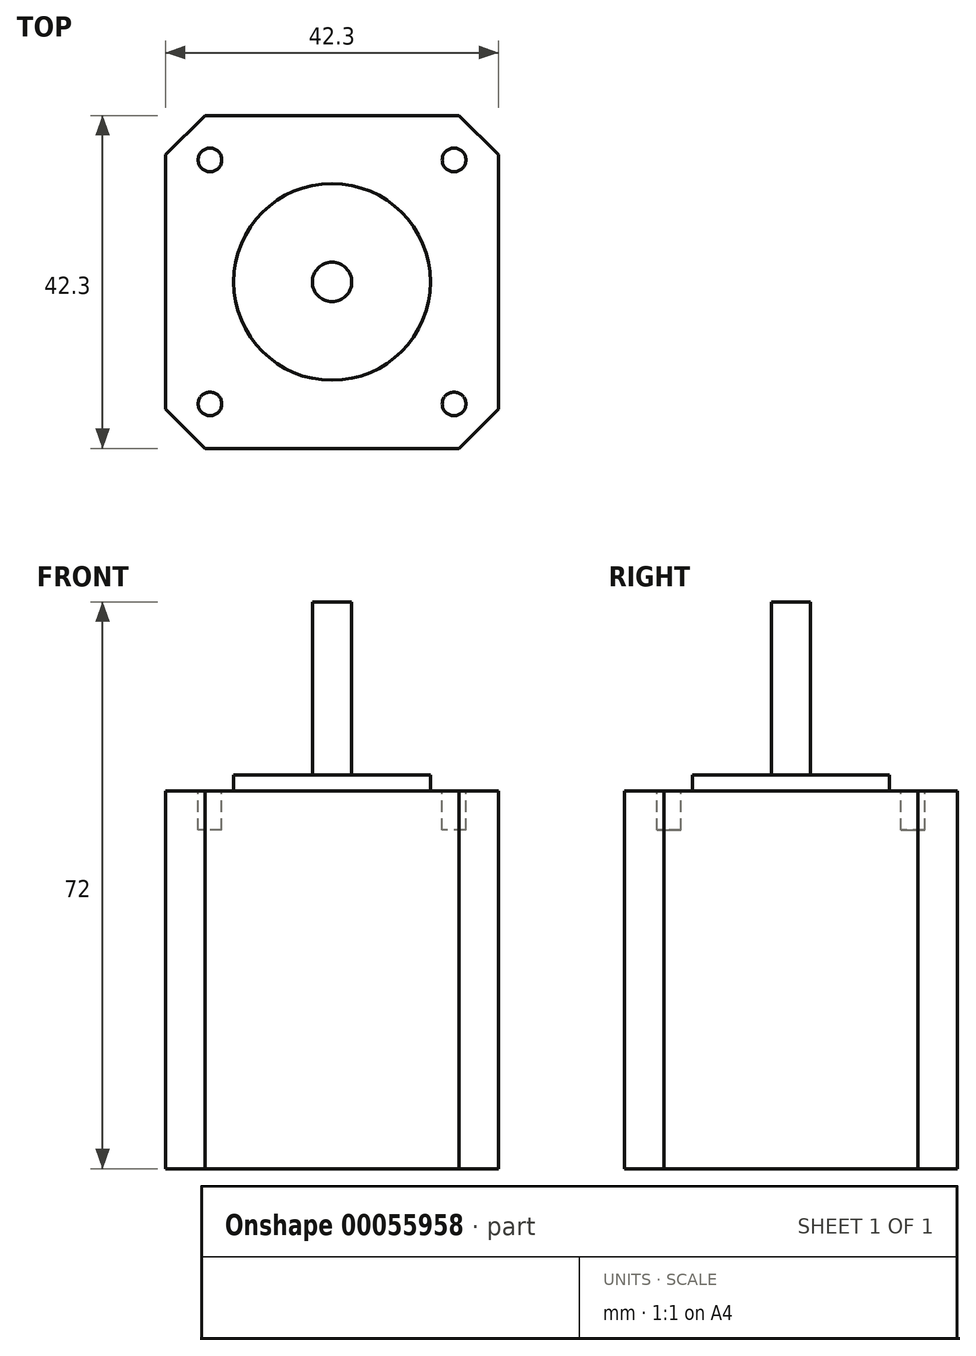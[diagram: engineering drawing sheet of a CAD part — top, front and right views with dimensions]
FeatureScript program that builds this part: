
annotation { "Feature Type Name" : "Feature", "Feature Type Description" : "" }
export const myFeature = defineFeature(function(context is Context, id is Id, definition is map)
    precondition{}
    {
        {
            var Q0;
            Q0=qCreatedBy(makeId("Top.planeOp"),FACE);
            var sketch = newSketch(context, id + "F0", { "sketchPlane" : qUnion([Q0])});
            skLineSegment(sketch, "E0.rect.bottom", {"start": v(21.15, 21.15) * mm, "end": v(-21.15, 21.15) * mm});
            skLineSegment(sketch, "E0.rect.top", {"start": v(21.15, -21.15) * mm, "end": v(-21.15, -21.15) * mm});
            skLineSegment(sketch, "E0.rect.left", {"start": v(21.15, 21.15) * mm, "end": v(21.15, -21.15) * mm});
            skLineSegment(sketch, "E0.rect.right", {"start": v(-21.15, 21.15) * mm, "end": v(-21.15, -21.15) * mm});
            skPoint(sketch, "E0.rect.middle", {"position": v(0, 0) * mm});
            skSolve(sketch);
        }
        {
            var Q0;
            Q0=makeQuery(id+"F0.imprint","IMPRINT",FACE,{"disambiguationData":[TD([[makeQuery(id+"F0.imprint","IMPRINT",EDGE,{"derivedFrom":sQuery(id+"F0.wireOp",EDGE,"E0.rect.bottom")}),1.0]])]});
            extrude(context, id + "F1", {"entities" : qUnion([Q0]), "depth" : 48 * mm});
        }
        {
            var Q0;
            Q0=makeQuery(id+"F1.opExtrude","CAP_FACE",FACE,{"disambiguationData":[OSD([sQuery(id+"F0.wireOp",EDGE,"E0.rect.bottom"),sQuery(id+"F0.wireOp",EDGE,"E0.rect.top"),sQuery(id+"F0.wireOp",EDGE,"E0.rect.left"),sQuery(id+"F0.wireOp",EDGE,"E0.rect.right")])],"isStart":false});
            var sketch = newSketch(context, id + "F2", { "sketchPlane" : qUnion([Q0])});
            skCircle(sketch, "E1", {"center": v(0, 0) * mm, "radius": 12.5 * mm});
            skSolve(sketch);
        }
        {
            var Q0;
            Q0=makeQuery(id+"F2.imprint","IMPRINT",FACE,{"disambiguationData":[TD([[makeQuery(id+"F2.imprint","IMPRINT",EDGE,{"derivedFrom":sQuery(id+"F2.wireOp",EDGE,"E1")}),1.0]])]});
            extrude(context, id + "F3", {"entities" : qUnion([Q0]), "operationType" : NewBodyOperationType.ADD, "depth" : 2 * mm});
        }
        {
            var Q0;
            Q0=makeQuery(id+"F3.opExtrude","CAP_FACE",FACE,{"disambiguationData":[OSD([sQuery(id+"F2.wireOp",EDGE,"E1")])],"isStart":false});
            var sketch = newSketch(context, id + "F4", { "sketchPlane" : qUnion([Q0])});
            skCircle(sketch, "E2", {"center": v(0, 0) * mm, "radius": 2.5 * mm});
            skSolve(sketch);
        }
        {
            var Q0;
            Q0=makeQuery(id+"F4.imprint","IMPRINT",FACE,{"disambiguationData":[TD([[makeQuery(id+"F4.imprint","IMPRINT",EDGE,{"derivedFrom":sQuery(id+"F4.wireOp",EDGE,"E2")}),1.0]])]});
            extrude(context, id + "F5", {"entities" : qUnion([Q0]), "operationType" : NewBodyOperationType.ADD, "depth" : 22 * mm});
        }
        {
            var Q0;
            Q0=makeQuery(id+"F1.opExtrude","CAP_FACE",FACE,{"disambiguationData":[OSD([sQuery(id+"F0.wireOp",EDGE,"E0.rect.bottom"),sQuery(id+"F0.wireOp",EDGE,"E0.rect.top"),sQuery(id+"F0.wireOp",EDGE,"E0.rect.left"),sQuery(id+"F0.wireOp",EDGE,"E0.rect.right")])],"isStart":false});
            var sketch = newSketch(context, id + "F6", { "sketchPlane" : qUnion([Q0])});
            skLineSegment(sketch, "E3.rect.bottom", {"start": v(15.5, 15.5) * mm, "end": v(-15.5, 15.5) * mm, "construction": true});
            skLineSegment(sketch, "E3.rect.top", {"start": v(15.5, -15.5) * mm, "end": v(-15.5, -15.5) * mm, "construction": true});
            skLineSegment(sketch, "E3.rect.left", {"start": v(15.5, 15.5) * mm, "end": v(15.5, -15.5) * mm, "construction": true});
            skLineSegment(sketch, "E3.rect.right", {"start": v(-15.5, 15.5) * mm, "end": v(-15.5, -15.5) * mm, "construction": true});
            skPoint(sketch, "E3.rect.middle", {"position": v(0, 0) * mm});
            skCircle(sketch, "E4", {"center": v(-15.5, 15.5) * mm, "radius": 1.5 * mm});
            skCircle(sketch, "E5", {"center": v(15.5, 15.5) * mm, "radius": 1.5 * mm});
            skCircle(sketch, "E6", {"center": v(15.5, -15.5) * mm, "radius": 1.5 * mm});
            skCircle(sketch, "E7", {"center": v(-15.5, -15.5) * mm, "radius": 1.5 * mm});
            skSolve(sketch);
        }
        {
            var Q0;
            Q0=makeQuery(id+"F6.imprint","IMPRINT",FACE,{"disambiguationData":[TD([[makeQuery(id+"F6.imprint","IMPRINT",EDGE,{"derivedFrom":sQuery(id+"F6.wireOp",EDGE,"E4")}),1.0]])]});
            var Q1;
            Q1=makeQuery(id+"F6.imprint","IMPRINT",FACE,{"disambiguationData":[TD([[makeQuery(id+"F6.imprint","IMPRINT",EDGE,{"derivedFrom":sQuery(id+"F6.wireOp",EDGE,"E5")}),1.0]])]});
            var Q2;
            Q2=makeQuery(id+"F6.imprint","IMPRINT",FACE,{"disambiguationData":[TD([[makeQuery(id+"F6.imprint","IMPRINT",EDGE,{"derivedFrom":sQuery(id+"F6.wireOp",EDGE,"E7")}),1.0]])]});
            var Q3;
            Q3=makeQuery(id+"F6.imprint","IMPRINT",FACE,{"disambiguationData":[TD([[makeQuery(id+"F6.imprint","IMPRINT",EDGE,{"derivedFrom":sQuery(id+"F6.wireOp",EDGE,"E6")}),1.0]])]});
            extrude(context, id + "F7", {"entities" : qUnion([Q0, Q1, Q2, Q3]), "operationType" : NewBodyOperationType.REMOVE, "oppositeDirection" : true, "depth" : 5 * mm});
        }
        {
            var Q0;
            Q0=makeQuery(id+"F1.opExtrude","SWEPT_EDGE",EDGE,{"disambiguationData":[OSD([sQuery(id+"F0.wireOp",EDGE,"E0.rect.top"),sQuery(id+"F0.wireOp",EDGE,"E0.rect.right")])]});
            var Q1;
            Q1=makeQuery(id+"F1.opExtrude","SWEPT_EDGE",EDGE,{"disambiguationData":[OSD([sQuery(id+"F0.wireOp",EDGE,"E0.rect.top"),sQuery(id+"F0.wireOp",EDGE,"E0.rect.left")])]});
            var Q2;
            Q2=makeQuery(id+"F1.opExtrude","SWEPT_EDGE",EDGE,{"disambiguationData":[OSD([sQuery(id+"F0.wireOp",EDGE,"E0.rect.bottom"),sQuery(id+"F0.wireOp",EDGE,"E0.rect.left")])]});
            var Q3;
            Q3=makeQuery(id+"F1.opExtrude","SWEPT_EDGE",EDGE,{"disambiguationData":[OSD([sQuery(id+"F0.wireOp",EDGE,"E0.rect.bottom"),sQuery(id+"F0.wireOp",EDGE,"E0.rect.right")])]});
            chamfer(context, id + "F8", {"entities" : qUnion([Q0, Q1, Q2, Q3]), "width" : 5 * mm, "tangentPropagation" : true});
        }
    });
